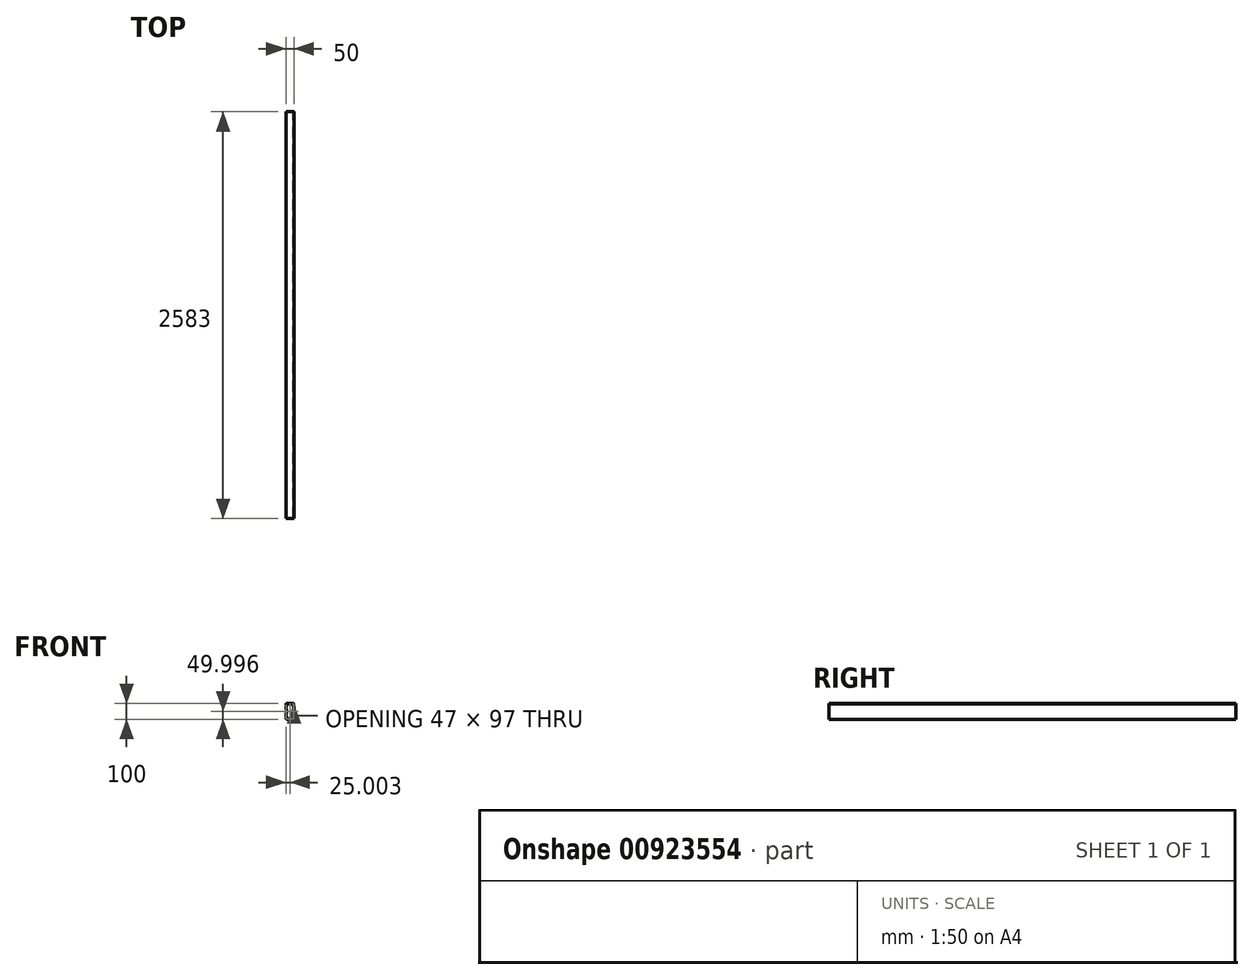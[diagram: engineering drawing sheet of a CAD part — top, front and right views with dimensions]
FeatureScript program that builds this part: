
annotation { "Feature Type Name" : "Feature", "Feature Type Description" : "" }
export const myFeature = defineFeature(function(context is Context, id is Id, definition is map)
    precondition{}
    {
        {
            var Q0;
            Q0=qCreatedBy(makeId("Front.planeOp"),FACE);
            var sketch = newSketch(context, id + "F0", { "sketchPlane" : qUnion([Q0])});
            skArc(sketch, "E0.filletArc", {"start": v(-71.4, 75.7) * mm, "mid": v(-75.16, 74.44) * mm, "end": v(-77.4, 71.17) * mm});
            skArc(sketch, "E1.filletArc", {"start": v(-77.4, -18.04) * mm, "mid": v(-75.58, -22.46) * mm, "end": v(-71.16, -24.3) * mm});
            skArc(sketch, "E2", {"start": v(-75.1, -12.5) * mm, "mid": v(-76.8, -15.04) * mm, "end": v(-77.4, -18.04) * mm});
            skArc(sketch, "E3", {"start": v(-74.4, -10.27) * mm, "mid": v(-75.2, -8.06) * mm, "end": v(-76.62, -6.19) * mm});
            skArc(sketch, "E4.filletArc", {"start": v(-75.1, -12.5) * mm, "mid": v(-74.48, -11.47) * mm, "end": v(-74.4, -10.27) * mm});
            skLineSegment(sketch, "E5", {"start": v(-77.4, -4.37) * mm, "end": v(-77.4, 11.38) * mm});
            skLineSegment(sketch, "E6", {"start": v(-77.4, 13.2) * mm, "end": v(-77.4, 13.2) * mm});
            skLineSegment(sketch, "E7", {"start": v(-74.9, 15.7) * mm, "end": v(-74.9, 35.7) * mm});
            skLineSegment(sketch, "E8", {"start": v(-77.4, 38.2) * mm, "end": v(-77.4, 38.2) * mm});
            skArc(sketch, "E9.filletArc", {"start": v(-76.16, 13.54) * mm, "mid": v(-75.24, 14.46) * mm, "end": v(-74.9, 15.7) * mm});
            skPoint(sketch, "E10.visualSharp", {"position": v(-77.4, 13.2) * mm});
            skArc(sketch, "E10.filletArc", {"start": v(-76.16, 13.54) * mm, "mid": v(-77.07, 12.63) * mm, "end": v(-77.4, 11.38) * mm});
            skArc(sketch, "E11.filletArc", {"start": v(-74.9, 35.7) * mm, "mid": v(-75.24, 36.96) * mm, "end": v(-76.16, 37.87) * mm});
            skPoint(sketch, "E12.visualSharp", {"position": v(-77.4, 38.2) * mm});
            skArc(sketch, "E12.filletArc", {"start": v(-77.4, 40.04) * mm, "mid": v(-77.07, 38.79) * mm, "end": v(-76.16, 37.87) * mm});
            skArc(sketch, "E13.filletArc", {"start": v(-77.4, -4.37) * mm, "mid": v(-77.2, -5.36) * mm, "end": v(-76.62, -6.19) * mm});
            skArc(sketch, "E14", {"start": v(-77.4, 71.17) * mm, "mid": v(-76.81, 68.18) * mm, "end": v(-75.12, 65.64) * mm});
            skArc(sketch, "E15", {"start": v(-76.65, 59.31) * mm, "mid": v(-75.23, 61.18) * mm, "end": v(-74.43, 63.38) * mm});
            skArc(sketch, "E16.filletArc", {"start": v(-74.43, 63.38) * mm, "mid": v(-74.5, 64.6) * mm, "end": v(-75.12, 65.64) * mm});
            skArc(sketch, "E17.filletArc", {"start": v(-76.65, 59.31) * mm, "mid": v(-77.2, 58.5) * mm, "end": v(-77.4, 57.52) * mm});
            skLineSegment(sketch, "E18", {"start": v(-77.4, 40.04) * mm, "end": v(-77.4, 57.52) * mm});
            skArc(sketch, "E19.MirrorCS", {"start": v(-27.4, 40.04) * mm, "mid": v(-27.74, 38.79) * mm, "end": v(-28.66, 37.87) * mm});
            skArc(sketch, "E20.MirrorCS", {"start": v(-29.9, 35.7) * mm, "mid": v(-29.57, 36.96) * mm, "end": v(-28.66, 37.87) * mm});
            skArc(sketch, "E21.MirrorCS", {"start": v(-28.66, 13.54) * mm, "mid": v(-29.57, 14.46) * mm, "end": v(-29.9, 15.7) * mm});
            skArc(sketch, "E22.MirrorCS", {"start": v(-28.66, 13.54) * mm, "mid": v(-27.74, 12.63) * mm, "end": v(-27.4, 11.38) * mm});
            skArc(sketch, "E23.MirrorCS", {"start": v(-28.16, 59.31) * mm, "mid": v(-27.6, 58.5) * mm, "end": v(-27.4, 57.52) * mm});
            skArc(sketch, "E24.MirrorCS", {"start": v(-29.71, -12.5) * mm, "mid": v(-30.34, -11.47) * mm, "end": v(-30.4, -10.27) * mm});
            skArc(sketch, "E25.MirrorCS", {"start": v(-27.4, -4.37) * mm, "mid": v(-27.61, -5.36) * mm, "end": v(-28.19, -6.19) * mm});
            skArc(sketch, "E26.MirrorCS", {"start": v(-30.38, 63.38) * mm, "mid": v(-30.32, 64.6) * mm, "end": v(-29.7, 65.64) * mm});
            skArc(sketch, "E27.MirrorCS", {"start": v(-28.16, 59.31) * mm, "mid": v(-29.58, 61.18) * mm, "end": v(-30.38, 63.38) * mm});
            skArc(sketch, "E28.MirrorCS", {"start": v(-30.4, -10.27) * mm, "mid": v(-29.62, -8.06) * mm, "end": v(-28.19, -6.19) * mm});
            skArc(sketch, "E29.MirrorCS", {"start": v(-27.4, 71.17) * mm, "mid": v(-28, 68.18) * mm, "end": v(-29.7, 65.64) * mm});
            skArc(sketch, "E30.MirrorCS", {"start": v(-29.71, -12.5) * mm, "mid": v(-28, -15.04) * mm, "end": v(-27.4, -18.04) * mm});
            skPoint(sketch, "E31.MirrorP", {"position": v(-15.15, 38.2) * mm});
            skArc(sketch, "E32.MirrorCS", {"start": v(-27.4, -18.04) * mm, "mid": v(-29.24, -22.46) * mm, "end": v(-33.66, -24.3) * mm});
            skArc(sketch, "E33.MirrorCS", {"start": v(-33.42, 75.7) * mm, "mid": v(-29.65, 74.44) * mm, "end": v(-27.4, 71.17) * mm});
            skPoint(sketch, "E34.MirrorP", {"position": v(-15.15, 58.67) * mm});
            skPoint(sketch, "E35.MirrorP", {"position": v(-17.65, 38.2) * mm});
            skLineSegment(sketch, "E36.MirrorCS", {"start": v(-27.4, 40.04) * mm, "end": v(-27.4, 57.52) * mm});
            skPoint(sketch, "E37.MirrorP", {"position": v(-18.27, 64.92) * mm});
            skLineSegment(sketch, "E38.MirrorCS", {"start": v(-27.4, -4.37) * mm, "end": v(-27.4, 11.38) * mm});
            skLineSegment(sketch, "E39.MirrorCS", {"start": v(-29.9, 15.7) * mm, "end": v(-29.9, 35.7) * mm});
            skLineSegment(sketch, "E40", {"start": v(-33.42, 75.7) * mm, "end": v(-71.4, 75.7) * mm});
            skLineSegment(sketch, "E41", {"start": v(-33.66, -24.3) * mm, "end": v(-71.16, -24.3) * mm});
            skSolve(sketch);
        }
        {
            var Q0;
            Q0=makeQuery(id+"F0.imprint","IMPRINT",FACE,{"disambiguationData":[TD([[makeQuery(id+"F0.imprint","IMPRINT",EDGE,{"derivedFrom":sQuery(id+"F0.wireOp",EDGE,"E0.filletArc")}),1.0]])]});
            extrude(context, id + "F1", {"entities" : qUnion([Q0]), "depth" : 2583 * mm, "offsetDistance" : 25 * mm});
        }
        {
            var Q0;
            Q0=makeQuery(id+"F1.opExtrude","CAP_FACE",FACE,{"disambiguationData":[OSD([sQuery(id+"F0.wireOp",EDGE,"E0.filletArc"),sQuery(id+"F0.wireOp",EDGE,"E1.filletArc"),sQuery(id+"F0.wireOp",EDGE,"E2"),sQuery(id+"F0.wireOp",EDGE,"E3"),sQuery(id+"F0.wireOp",EDGE,"E4.filletArc"),sQuery(id+"F0.wireOp",EDGE,"E5"),sQuery(id+"F0.wireOp",EDGE,"E7"),sQuery(id+"F0.wireOp",EDGE,"E9.filletArc"),sQuery(id+"F0.wireOp",EDGE,"E10.filletArc"),sQuery(id+"F0.wireOp",EDGE,"E11.filletArc"),sQuery(id+"F0.wireOp",EDGE,"E12.filletArc"),sQuery(id+"F0.wireOp",EDGE,"E13.filletArc"),sQuery(id+"F0.wireOp",EDGE,"E14"),sQuery(id+"F0.wireOp",EDGE,"E15"),sQuery(id+"F0.wireOp",EDGE,"E16.filletArc"),sQuery(id+"F0.wireOp",EDGE,"E17.filletArc"),sQuery(id+"F0.wireOp",EDGE,"E18"),sQuery(id+"F0.wireOp",EDGE,"E19.MirrorCS"),sQuery(id+"F0.wireOp",EDGE,"E20.MirrorCS"),sQuery(id+"F0.wireOp",EDGE,"E21.MirrorCS"),sQuery(id+"F0.wireOp",EDGE,"E22.MirrorCS"),sQuery(id+"F0.wireOp",EDGE,"E23.MirrorCS"),sQuery(id+"F0.wireOp",EDGE,"E24.MirrorCS"),sQuery(id+"F0.wireOp",EDGE,"E25.MirrorCS"),sQuery(id+"F0.wireOp",EDGE,"E26.MirrorCS"),sQuery(id+"F0.wireOp",EDGE,"E27.MirrorCS"),sQuery(id+"F0.wireOp",EDGE,"E28.MirrorCS"),sQuery(id+"F0.wireOp",EDGE,"E29.MirrorCS"),sQuery(id+"F0.wireOp",EDGE,"E30.MirrorCS"),sQuery(id+"F0.wireOp",EDGE,"E32.MirrorCS"),sQuery(id+"F0.wireOp",EDGE,"E33.MirrorCS"),sQuery(id+"F0.wireOp",EDGE,"E36.MirrorCS"),sQuery(id+"F0.wireOp",EDGE,"E38.MirrorCS"),sQuery(id+"F0.wireOp",EDGE,"E39.MirrorCS"),sQuery(id+"F0.wireOp",EDGE,"E40"),sQuery(id+"F0.wireOp",EDGE,"E41")])],"isStart":true});
            shell(context, id + "F2", {"entities" : qUnion([Q0]), "thickness" : 1.5 * mm});
        }
        {
            var Q0;
            Q0=makeQuery(id+"F1.opExtrude","CAP_FACE",FACE,{"disambiguationData":[OSD([sQuery(id+"F0.wireOp",EDGE,"E0.filletArc"),sQuery(id+"F0.wireOp",EDGE,"E1.filletArc"),sQuery(id+"F0.wireOp",EDGE,"E2"),sQuery(id+"F0.wireOp",EDGE,"E3"),sQuery(id+"F0.wireOp",EDGE,"E4.filletArc"),sQuery(id+"F0.wireOp",EDGE,"E5"),sQuery(id+"F0.wireOp",EDGE,"E7"),sQuery(id+"F0.wireOp",EDGE,"E9.filletArc"),sQuery(id+"F0.wireOp",EDGE,"E10.filletArc"),sQuery(id+"F0.wireOp",EDGE,"E11.filletArc"),sQuery(id+"F0.wireOp",EDGE,"E12.filletArc"),sQuery(id+"F0.wireOp",EDGE,"E13.filletArc"),sQuery(id+"F0.wireOp",EDGE,"E14"),sQuery(id+"F0.wireOp",EDGE,"E15"),sQuery(id+"F0.wireOp",EDGE,"E16.filletArc"),sQuery(id+"F0.wireOp",EDGE,"E17.filletArc"),sQuery(id+"F0.wireOp",EDGE,"E18"),sQuery(id+"F0.wireOp",EDGE,"E19.MirrorCS"),sQuery(id+"F0.wireOp",EDGE,"E20.MirrorCS"),sQuery(id+"F0.wireOp",EDGE,"E21.MirrorCS"),sQuery(id+"F0.wireOp",EDGE,"E22.MirrorCS"),sQuery(id+"F0.wireOp",EDGE,"E23.MirrorCS"),sQuery(id+"F0.wireOp",EDGE,"E24.MirrorCS"),sQuery(id+"F0.wireOp",EDGE,"E25.MirrorCS"),sQuery(id+"F0.wireOp",EDGE,"E26.MirrorCS"),sQuery(id+"F0.wireOp",EDGE,"E27.MirrorCS"),sQuery(id+"F0.wireOp",EDGE,"E28.MirrorCS"),sQuery(id+"F0.wireOp",EDGE,"E29.MirrorCS"),sQuery(id+"F0.wireOp",EDGE,"E30.MirrorCS"),sQuery(id+"F0.wireOp",EDGE,"E32.MirrorCS"),sQuery(id+"F0.wireOp",EDGE,"E33.MirrorCS"),sQuery(id+"F0.wireOp",EDGE,"E36.MirrorCS"),sQuery(id+"F0.wireOp",EDGE,"E38.MirrorCS"),sQuery(id+"F0.wireOp",EDGE,"E39.MirrorCS"),sQuery(id+"F0.wireOp",EDGE,"E40"),sQuery(id+"F0.wireOp",EDGE,"E41")])],"isStart":false});
            var Q1;
            Q1=makeQuery(id+"F2.opShell","OFFSET_FACE",FACE,{"disambiguationData":[OSD([sQuery(id+"F0.wireOp",EDGE,"E0.filletArc"),sQuery(id+"F0.wireOp",EDGE,"E1.filletArc"),sQuery(id+"F0.wireOp",EDGE,"E2"),sQuery(id+"F0.wireOp",EDGE,"E3"),sQuery(id+"F0.wireOp",EDGE,"E4.filletArc"),sQuery(id+"F0.wireOp",EDGE,"E5"),sQuery(id+"F0.wireOp",EDGE,"E7"),sQuery(id+"F0.wireOp",EDGE,"E9.filletArc"),sQuery(id+"F0.wireOp",EDGE,"E10.filletArc"),sQuery(id+"F0.wireOp",EDGE,"E11.filletArc"),sQuery(id+"F0.wireOp",EDGE,"E12.filletArc"),sQuery(id+"F0.wireOp",EDGE,"E13.filletArc"),sQuery(id+"F0.wireOp",EDGE,"E14"),sQuery(id+"F0.wireOp",EDGE,"E15"),sQuery(id+"F0.wireOp",EDGE,"E16.filletArc"),sQuery(id+"F0.wireOp",EDGE,"E17.filletArc"),sQuery(id+"F0.wireOp",EDGE,"E18"),sQuery(id+"F0.wireOp",EDGE,"E19.MirrorCS"),sQuery(id+"F0.wireOp",EDGE,"E20.MirrorCS"),sQuery(id+"F0.wireOp",EDGE,"E21.MirrorCS"),sQuery(id+"F0.wireOp",EDGE,"E22.MirrorCS"),sQuery(id+"F0.wireOp",EDGE,"E23.MirrorCS"),sQuery(id+"F0.wireOp",EDGE,"E24.MirrorCS"),sQuery(id+"F0.wireOp",EDGE,"E25.MirrorCS"),sQuery(id+"F0.wireOp",EDGE,"E26.MirrorCS"),sQuery(id+"F0.wireOp",EDGE,"E27.MirrorCS"),sQuery(id+"F0.wireOp",EDGE,"E28.MirrorCS"),sQuery(id+"F0.wireOp",EDGE,"E29.MirrorCS"),sQuery(id+"F0.wireOp",EDGE,"E30.MirrorCS"),sQuery(id+"F0.wireOp",EDGE,"E32.MirrorCS"),sQuery(id+"F0.wireOp",EDGE,"E33.MirrorCS"),sQuery(id+"F0.wireOp",EDGE,"E36.MirrorCS"),sQuery(id+"F0.wireOp",EDGE,"E38.MirrorCS"),sQuery(id+"F0.wireOp",EDGE,"E39.MirrorCS"),sQuery(id+"F0.wireOp",EDGE,"E40"),sQuery(id+"F0.wireOp",EDGE,"E41")])]});
            shell(context, id + "F3", {"entities" : qUnion([Q0, Q1]), "thickness" : 1.5 * mm});
        }
    });
